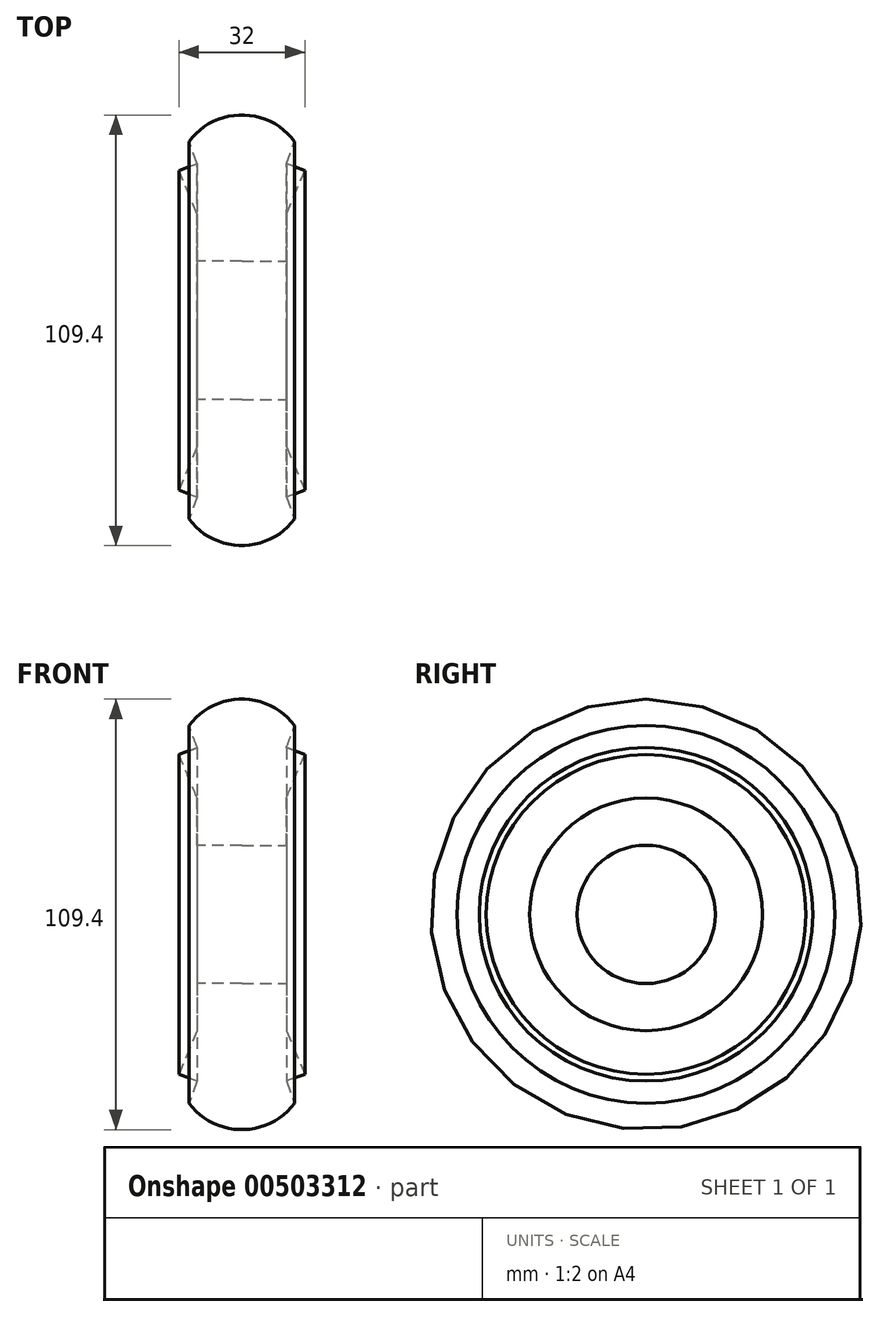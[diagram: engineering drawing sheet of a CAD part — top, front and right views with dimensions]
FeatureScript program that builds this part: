
annotation { "Feature Type Name" : "Feature", "Feature Type Description" : "" }
export const myFeature = defineFeature(function(context is Context, id is Id, definition is map)
    precondition{}
    {
        {
            var Q0;
            Q0=qCreatedBy(makeId("Front.planeOp"),FACE);
            var sketch = newSketch(context, id + "F0", { "sketchPlane" : qUnion([Q0])});
            skLineSegment(sketch, "E0", {"start": v(0, 65.65) * mm, "end": v(0, -70.9) * mm, "construction": true});
            skLineSegment(sketch, "E1", {"start": v(13.41, 47.99) * mm, "end": v(11.32, 42.36) * mm});
            skLineSegment(sketch, "E2", {"start": v(11.32, 42.36) * mm, "end": v(16, 40.62) * mm});
            skLineSegment(sketch, "E3", {"start": v(16, 40.62) * mm, "end": v(11.32, 29.57) * mm});
            skLineSegment(sketch, "E4", {"start": v(11.32, 29.57) * mm, "end": v(0, 29.54) * mm});
            skLineSegment(sketch, "E5.MirrorCS", {"start": v(-11.32, 29.57) * mm, "end": v(0, 29.54) * mm});
            skLineSegment(sketch, "E6.MirrorCS", {"start": v(-16, 40.62) * mm, "end": v(-11.32, 29.57) * mm});
            skLineSegment(sketch, "E7.MirrorCS", {"start": v(-13.41, 47.99) * mm, "end": v(-11.32, 42.36) * mm});
            skLineSegment(sketch, "E8.MirrorCS", {"start": v(-11.32, 42.36) * mm, "end": v(-16, 40.62) * mm});
            skLineSegment(sketch, "E9", {"start": v(11.32, 29.57) * mm, "end": v(11.34, 17.57) * mm});
            skLineSegment(sketch, "E10", {"start": v(11.34, 17.57) * mm, "end": v(0, 17.54) * mm});
            skLineSegment(sketch, "E11.MirrorCS", {"start": v(-11.32, 29.57) * mm, "end": v(-11.34, 17.57) * mm});
            skLineSegment(sketch, "E12.MirrorCS", {"start": v(-11.34, 17.57) * mm, "end": v(0, 17.54) * mm});
            skLineSegment(sketch, "E13", {"start": v(-65.17, 0) * mm, "end": v(72.9, 0) * mm, "construction": true});
            skArc(sketch, "E14", {"start": v(13.41, 47.99) * mm, "mid": v(0, 54.7) * mm, "end": v(-13.41, 47.99) * mm});
            skPoint(sketch, "E15", {"position": v(0, 54.7) * mm});
            skSolve(sketch);
        }
        {
            var Q0;
            Q0=makeQuery(id+"F0.imprint","IMPRINT",FACE,{"disambiguationData":[TD([[makeQuery(id+"F0.imprint","IMPRINT",EDGE,{"derivedFrom":sQuery(id+"F0.wireOp",EDGE,"E4")}),1.0]])]});
            var Q1;
            Q1=makeQuery(id+"F0.imprint","IMPRINT",FACE,{"disambiguationData":[TD([[makeQuery(id+"F0.imprint","IMPRINT",EDGE,{"derivedFrom":sQuery(id+"F0.wireOp",EDGE,"E1")}),-1.0]])]});
            var Q2;
            Q2=sQuery(id+"F0.wireOp",EDGE,"E13");
            revolve(context, id + "F1", {"entities" : qUnion([Q0, Q1]), "axis" : qUnion([Q2]), "revolveType" : RevolveType.FULL});
        }
    });
